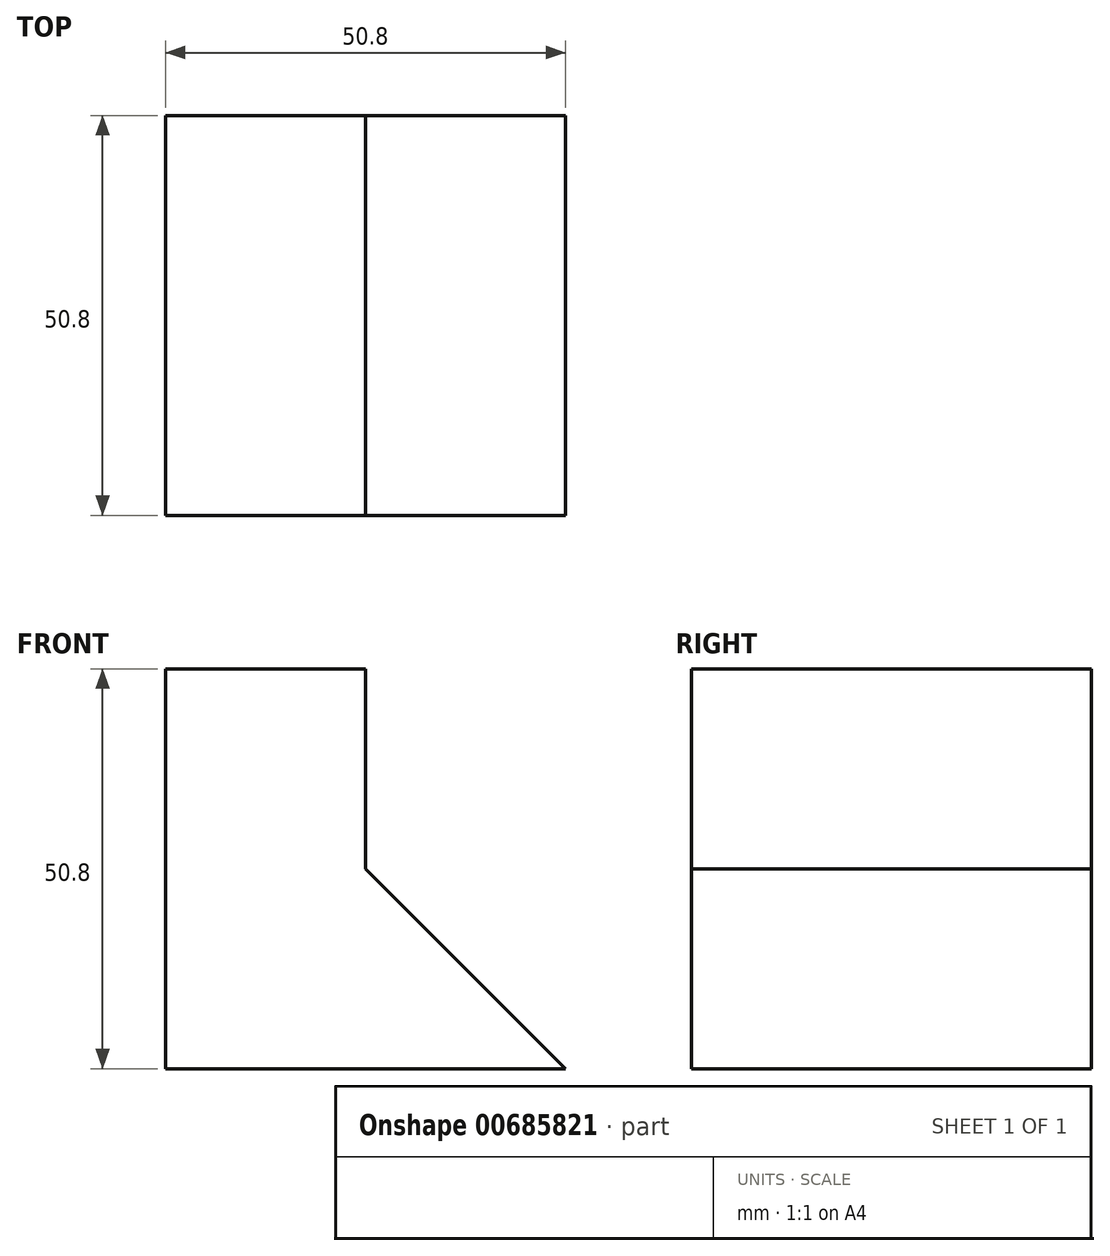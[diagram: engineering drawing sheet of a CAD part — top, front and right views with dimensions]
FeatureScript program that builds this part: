
annotation { "Feature Type Name" : "Feature", "Feature Type Description" : "" }
export const myFeature = defineFeature(function(context is Context, id is Id, definition is map)
    precondition{}
    {
        {
            var Q0;
            Q0=qCreatedBy(makeId("Front.planeOp"),FACE);
            var sketch = newSketch(context, id + "F0", { "sketchPlane" : qUnion([Q0])});
            skLineSegment(sketch, "E0", {"start": v(-49.36, 29.32) * mm, "end": v(-49.36, -21.48) * mm});
            skLineSegment(sketch, "E1", {"start": v(-49.36, 29.32) * mm, "end": v(-23.96, 29.32) * mm});
            skLineSegment(sketch, "E2", {"start": v(-23.96, 29.32) * mm, "end": v(-23.96, 3.92) * mm});
            skLineSegment(sketch, "E3", {"start": v(-49.36, -21.48) * mm, "end": v(1.44, -21.48) * mm});
            skLineSegment(sketch, "E4", {"start": v(-23.96, 3.92) * mm, "end": v(1.44, -21.48) * mm});
            skSolve(sketch);
        }
        {
            var Q0;
            Q0 = qSketchRegion(id + "F0", true);
            extrude(context, id + "F1", {"entities" : qUnion([Q0]), "depth" : 50.8 * mm, "offsetDistance" : 25.4 * mm});
        }
    });
